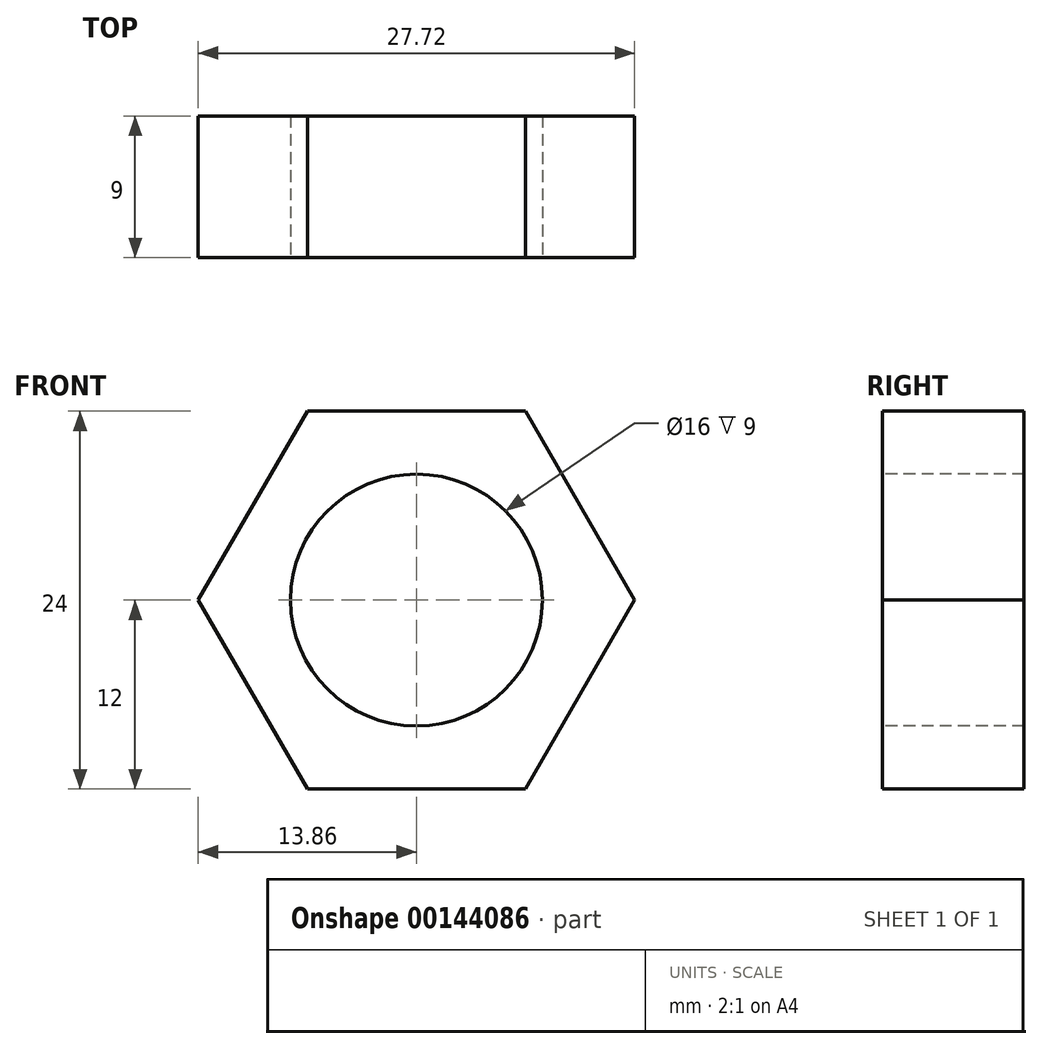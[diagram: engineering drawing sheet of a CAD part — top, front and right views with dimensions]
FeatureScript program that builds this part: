
annotation { "Feature Type Name" : "Feature", "Feature Type Description" : "" }
export const myFeature = defineFeature(function(context is Context, id is Id, definition is map)
    precondition{}
    {
        {
            var Q0;
            Q0=qCreatedBy(makeId("Front.planeOp"),FACE);
            var sketch = newSketch(context, id + "F0", { "sketchPlane" : qUnion([Q0])});
            skCircle(sketch, "E0.cCircle", {"center": v(0, 0) * mm, "radius": 12 * mm, "construction": true});
            skLineSegment(sketch, "E0.0", {"start": v(-6.93, 12) * mm, "end": v(6.93, 12) * mm});
            skLineSegment(sketch, "E0.1", {"start": v(6.93, 12) * mm, "end": v(13.86, 0) * mm});
            skLineSegment(sketch, "E0.2", {"start": v(13.86, 0) * mm, "end": v(6.93, -12) * mm});
            skLineSegment(sketch, "E0.3", {"start": v(6.93, -12) * mm, "end": v(-6.93, -12) * mm});
            skLineSegment(sketch, "E0.4", {"start": v(-6.93, -12) * mm, "end": v(-13.86, 0) * mm});
            skLineSegment(sketch, "E0.5", {"start": v(-13.86, 0) * mm, "end": v(-6.93, 12) * mm});
            skPoint(sketch, "E0.0.midPoint", {"position": v(0, 12) * mm});
            skSolve(sketch);
        }
        {
            var Q0;
            Q0 = qSketchRegion(id + "F0", true);
            extrude(context, id + "F1", {"entities" : qUnion([Q0]), "oppositeDirection" : true, "depth" : 9 * mm});
        }
        {
            var Q0;
            Q0=makeQuery(id+"F1.opExtrude","CAP_FACE",FACE,{"disambiguationData":[OSD([sQuery(id+"F0.wireOp",EDGE,"E0.0"),sQuery(id+"F0.wireOp",EDGE,"E0.1"),sQuery(id+"F0.wireOp",EDGE,"E0.2"),sQuery(id+"F0.wireOp",EDGE,"E0.3"),sQuery(id+"F0.wireOp",EDGE,"E0.4"),sQuery(id+"F0.wireOp",EDGE,"E0.5")])],"isStart":true});
            var sketch = newSketch(context, id + "F2", { "sketchPlane" : qUnion([Q0])});
            skCircle(sketch, "E1", {"center": v(0, 0) * mm, "radius": 8 * mm});
            skSolve(sketch);
        }
        {
            var Q0;
            Q0 = qSketchRegion(id + "F2", true);
            extrude(context, id + "F3", {"entities" : qUnion([Q0]), "operationType" : NewBodyOperationType.REMOVE, "endBound" : BoundingType.THROUGH_ALL, "oppositeDirection" : true, "depth" : 25 * mm});
        }
    });
